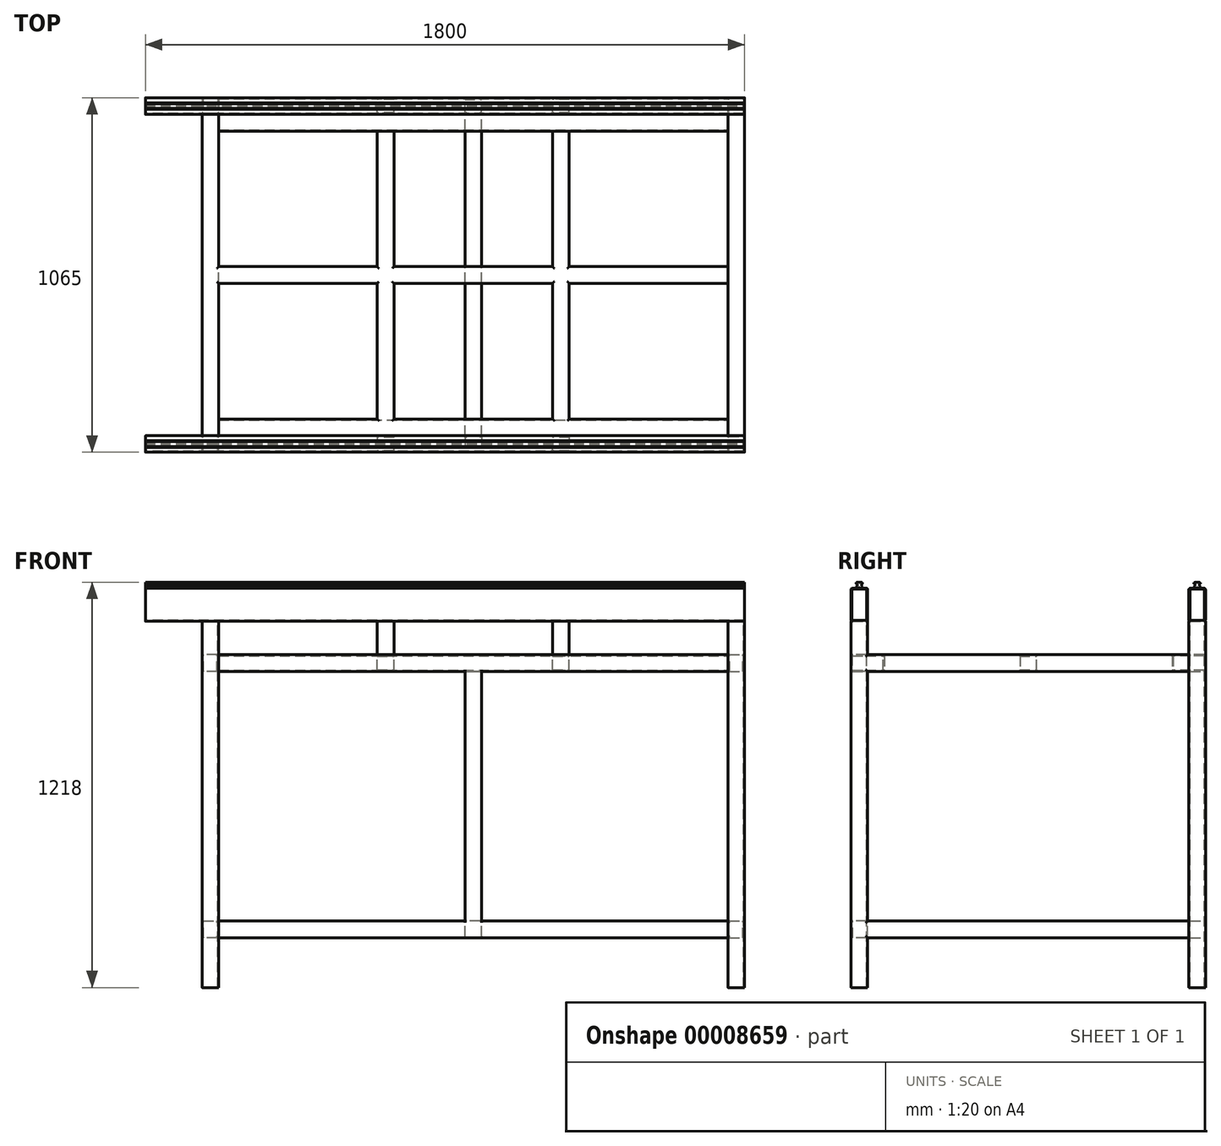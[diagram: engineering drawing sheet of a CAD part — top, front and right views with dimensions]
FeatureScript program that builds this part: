
annotation { "Feature Type Name" : "Feature", "Feature Type Description" : "" }
export const myFeature = defineFeature(function(context is Context, id is Id, definition is map)
    precondition{}
    {
        {
            var Q0;
            Q0=qCreatedBy(makeId("Right.planeOp"),FACE);
            var sketch = newSketch(context, id + "F0", { "sketchPlane" : qUnion([Q0])});
            skLineSegment(sketch, "E0.rect.bottom", {"start": v(20, 50) * mm, "end": v(-20, 50) * mm});
            skLineSegment(sketch, "E0.rect.top", {"start": v(20, -50) * mm, "end": v(-20, -50) * mm});
            skLineSegment(sketch, "E0.rect.left", {"start": v(25, 45) * mm, "end": v(25, -45) * mm});
            skLineSegment(sketch, "E0.rect.right", {"start": v(-25, 45) * mm, "end": v(-25, -45) * mm});
            skPoint(sketch, "E0.rect.middle", {"position": v(0, 0) * mm});
            skPoint(sketch, "E1.visualSharp", {"position": v(-25, 50) * mm});
            skArc(sketch, "E1.filletArc", {"start": v(-20, 50) * mm, "mid": v(-23.54, 48.54) * mm, "end": v(-25, 45) * mm});
            skPoint(sketch, "E2.visualSharp", {"position": v(25, 50) * mm});
            skArc(sketch, "E2.filletArc", {"start": v(25, 45) * mm, "mid": v(23.54, 48.54) * mm, "end": v(20, 50) * mm});
            skPoint(sketch, "E3.visualSharp", {"position": v(25, -50) * mm});
            skArc(sketch, "E3.filletArc", {"start": v(20, -50) * mm, "mid": v(23.54, -48.54) * mm, "end": v(25, -45) * mm});
            skPoint(sketch, "E4.visualSharp", {"position": v(-25, -50) * mm});
            skArc(sketch, "E4.filletArc", {"start": v(-25, -45) * mm, "mid": v(-23.54, -48.54) * mm, "end": v(-20, -50) * mm});
            skLineSegment(sketch, "E5.0", {"start": v(-22, 47) * mm, "end": v(-22, -47) * mm});
            skLineSegment(sketch, "E5.1", {"start": v(22, 47) * mm, "end": v(-22, 47) * mm});
            skLineSegment(sketch, "E5.2", {"start": v(22, 47) * mm, "end": v(22, -47) * mm});
            skLineSegment(sketch, "E5.3", {"start": v(22, -47) * mm, "end": v(-22, -47) * mm});
            skSolve(sketch);
        }
        {
            var Q0;
            Q0=qCreatedBy(makeId("Right.planeOp"),FACE);
            var sketch = newSketch(context, id + "F1", { "sketchPlane" : qUnion([Q0])});
            skLineSegment(sketch, "E6.rect.bottom", {"start": v(-995, 50) * mm, "end": v(-1035, 50) * mm});
            skLineSegment(sketch, "E6.rect.top", {"start": v(-995, -50) * mm, "end": v(-1035, -50) * mm});
            skLineSegment(sketch, "E6.rect.left", {"start": v(-990, 45) * mm, "end": v(-990, -45) * mm});
            skLineSegment(sketch, "E6.rect.right", {"start": v(-1040, 45) * mm, "end": v(-1040, -45) * mm});
            skPoint(sketch, "E6.rect.middle", {"position": v(0, 0) * mm});
            skPoint(sketch, "E7.visualSharp", {"position": v(-1040, 50) * mm});
            skArc(sketch, "E7.filletArc", {"start": v(-1035, 50) * mm, "mid": v(-1038.54, 48.54) * mm, "end": v(-1040, 45) * mm});
            skPoint(sketch, "E8.visualSharp", {"position": v(-990, 50) * mm});
            skArc(sketch, "E8.filletArc", {"start": v(-990, 45) * mm, "mid": v(-991.46, 48.54) * mm, "end": v(-995, 50) * mm});
            skPoint(sketch, "E9.visualSharp", {"position": v(-990, -50) * mm});
            skArc(sketch, "E9.filletArc", {"start": v(-995, -50) * mm, "mid": v(-991.46, -48.54) * mm, "end": v(-990, -45) * mm});
            skPoint(sketch, "E10.visualSharp", {"position": v(-1040, -50) * mm});
            skArc(sketch, "E10.filletArc", {"start": v(-1040, -45) * mm, "mid": v(-1038.54, -48.54) * mm, "end": v(-1035, -50) * mm});
            skLineSegment(sketch, "E11.0", {"start": v(-1037, 47) * mm, "end": v(-1037, -47) * mm});
            skLineSegment(sketch, "E11.1", {"start": v(-993, 47) * mm, "end": v(-1037, 47) * mm});
            skLineSegment(sketch, "E11.2", {"start": v(-993, 47) * mm, "end": v(-993, -47) * mm});
            skLineSegment(sketch, "E11.3", {"start": v(-993, -47) * mm, "end": v(-1037, -47) * mm});
            skSolve(sketch);
        }
        {
            var Q0;
            Q0=makeQuery(id+"F1.imprint","IMPRINT",FACE,{"disambiguationData":[TD([[makeQuery(id+"F1.imprint","IMPRINT",EDGE,{"derivedFrom":sQuery(id+"F1.wireOp",EDGE,"E6.rect.bottom")}),1.0]])]});
            var Q1;
            Q1=makeQuery(id+"F0.imprint","IMPRINT",FACE,{"disambiguationData":[TD([[makeQuery(id+"F0.imprint","IMPRINT",EDGE,{"derivedFrom":sQuery(id+"F0.wireOp",EDGE,"E0.rect.bottom")}),1.0]])]});
            extrude(context, id + "F2", {"entities" : qUnion([Q0, Q1]), "depth" : 1800 * mm});
        }
        {
            var Q0;
            Q0=makeQuery(id+"F2.opExtrude","CAP_FACE",FACE,{"disambiguationData":[OSD([sQuery(id+"F1.wireOp",EDGE,"E6.rect.bottom"),sQuery(id+"F1.wireOp",EDGE,"E6.rect.top"),sQuery(id+"F1.wireOp",EDGE,"E6.rect.left"),sQuery(id+"F1.wireOp",EDGE,"E6.rect.right"),sQuery(id+"F1.wireOp",EDGE,"E7.filletArc"),sQuery(id+"F1.wireOp",EDGE,"E8.filletArc"),sQuery(id+"F1.wireOp",EDGE,"E9.filletArc"),sQuery(id+"F1.wireOp",EDGE,"E10.filletArc"),sQuery(id+"F1.wireOp",EDGE,"E11.0"),sQuery(id+"F1.wireOp",EDGE,"E11.1"),sQuery(id+"F1.wireOp",EDGE,"E11.2"),sQuery(id+"F1.wireOp",EDGE,"E11.3")])],"isStart":false});
            cPlane(context, id + "F3", {"entities" : qUnion([Q0]), "cplaneType" : CPlaneType.OFFSET, "offset" : 50 * mm, "oppositeDirection" : true, "width" : 150 * mm, "height" : 150 * mm});
        }
        {
            var Q0;
            Q0=qCreatedBy(id+"F3.planeOp",FACE);
            var sketch = newSketch(context, id + "F4", { "sketchPlane" : qUnion([Q0])});
            skLineSegment(sketch, "E12.bottom", {"start": v(-1035, -150) * mm, "end": v(-945, -150) * mm});
            skLineSegment(sketch, "E12.top", {"start": v(-1035, -200) * mm, "end": v(-945, -200) * mm});
            skLineSegment(sketch, "E12.left", {"start": v(-1040, -155) * mm, "end": v(-1040, -195) * mm});
            skLineSegment(sketch, "E12.right", {"start": v(-940, -155) * mm, "end": v(-940, -195) * mm});
            skPoint(sketch, "E13.visualSharp", {"position": v(-1040, -150) * mm});
            skArc(sketch, "E13.filletArc", {"start": v(-1035, -150) * mm, "mid": v(-1038.54, -151.46) * mm, "end": v(-1040, -155) * mm});
            skPoint(sketch, "E14.visualSharp", {"position": v(-940, -150) * mm});
            skArc(sketch, "E14.filletArc", {"start": v(-940, -155) * mm, "mid": v(-941.46, -151.46) * mm, "end": v(-945, -150) * mm});
            skPoint(sketch, "E15.visualSharp", {"position": v(-940, -200) * mm});
            skArc(sketch, "E15.filletArc", {"start": v(-945, -200) * mm, "mid": v(-941.46, -198.54) * mm, "end": v(-940, -195) * mm});
            skPoint(sketch, "E16.visualSharp", {"position": v(-1040, -200) * mm});
            skArc(sketch, "E16.filletArc", {"start": v(-1040, -195) * mm, "mid": v(-1038.54, -198.54) * mm, "end": v(-1035, -200) * mm});
            skLineSegment(sketch, "E17.0", {"start": v(-995, -50) * mm, "end": v(-1035, -50) * mm});
            skLineSegment(sketch, "E18.0", {"start": v(-1040, 45) * mm, "end": v(-1040, -45) * mm});
            skLineSegment(sketch, "E19.0", {"start": v(-943, -153) * mm, "end": v(-943, -197) * mm});
            skLineSegment(sketch, "E19.1", {"start": v(-1037, -153) * mm, "end": v(-943, -153) * mm});
            skLineSegment(sketch, "E19.2", {"start": v(-1037, -153) * mm, "end": v(-1037, -197) * mm});
            skLineSegment(sketch, "E19.3", {"start": v(-1037, -197) * mm, "end": v(-943, -197) * mm});
            skLineSegment(sketch, "E20.bottom", {"start": v(20, -150) * mm, "end": v(-70, -150) * mm});
            skLineSegment(sketch, "E20.top", {"start": v(20, -200) * mm, "end": v(-70, -200) * mm});
            skLineSegment(sketch, "E20.left", {"start": v(25, -155) * mm, "end": v(25, -195) * mm});
            skLineSegment(sketch, "E20.right", {"start": v(-75, -155) * mm, "end": v(-75, -195) * mm});
            skPoint(sketch, "E21.0", {"position": v(25, -50) * mm});
            skPoint(sketch, "E22.visualSharp", {"position": v(-75, -150) * mm});
            skArc(sketch, "E22.filletArc", {"start": v(-70, -150) * mm, "mid": v(-73.54, -151.46) * mm, "end": v(-75, -155) * mm});
            skPoint(sketch, "E23.visualSharp", {"position": v(25, -200) * mm});
            skArc(sketch, "E23.filletArc", {"start": v(20, -200) * mm, "mid": v(23.54, -198.54) * mm, "end": v(25, -195) * mm});
            skPoint(sketch, "E24.visualSharp", {"position": v(25, -150) * mm});
            skArc(sketch, "E24.filletArc", {"start": v(25, -155) * mm, "mid": v(23.54, -151.46) * mm, "end": v(20, -150) * mm});
            skPoint(sketch, "E25.visualSharp", {"position": v(-75, -200) * mm});
            skArc(sketch, "E25.filletArc", {"start": v(-75, -195) * mm, "mid": v(-73.54, -198.54) * mm, "end": v(-70, -200) * mm});
            skLineSegment(sketch, "E26.0", {"start": v(22, -153) * mm, "end": v(-72, -153) * mm});
            skLineSegment(sketch, "E26.1", {"start": v(22, -153) * mm, "end": v(22, -197) * mm});
            skLineSegment(sketch, "E26.2", {"start": v(22, -197) * mm, "end": v(-72, -197) * mm});
            skLineSegment(sketch, "E26.3", {"start": v(-72, -153) * mm, "end": v(-72, -197) * mm});
            skSolve(sketch);
        }
        {
            var Q0;
            Q0=makeQuery(id+"F4.imprint","IMPRINT",FACE,{"disambiguationData":[TD([[makeQuery(id+"F4.imprint","IMPRINT",EDGE,{"derivedFrom":sQuery(id+"F4.wireOp",EDGE,"E12.bottom")}),-1.0]])]});
            var Q1;
            Q1=makeQuery(id+"F4.imprint","IMPRINT",FACE,{"disambiguationData":[TD([[makeQuery(id+"F4.imprint","IMPRINT",EDGE,{"derivedFrom":sQuery(id+"F4.wireOp",EDGE,"E20.bottom")}),1.0]])]});
            extrude(context, id + "F5", {"entities" : qUnion([Q0, Q1]), "oppositeDirection" : true, "depth" : 1530 * mm});
        }
        {
            var Q0;
            Q0=makeQuery(id+"F2.opExtrude","SWEPT_FACE",FACE,{"disambiguationData":[OSD([sQuery(id+"F1.wireOp",EDGE,"E6.rect.top")])]});
            cPlane(context, id + "F6", {"entities" : qUnion([Q0]), "cplaneType" : CPlaneType.OFFSET, "offset" : 0 * mm, "width" : 150 * mm, "height" : 150 * mm});
        }
        {
            var Q0;
            Q0=qCreatedBy(id+"F6.planeOp",FACE);
            var sketch = newSketch(context, id + "F7", { "sketchPlane" : qUnion([Q0])});
            skPoint(sketch, "E27.0", {"position": v(1800, 990) * mm});
            skPoint(sketch, "E28.0", {"position": v(1750, 1040) * mm});
            skLineSegment(sketch, "E29.bottom", {"start": v(1755, 1040) * mm, "end": v(1795, 1040) * mm});
            skLineSegment(sketch, "E29.top", {"start": v(1755, 990) * mm, "end": v(1795, 990) * mm});
            skLineSegment(sketch, "E29.left", {"start": v(1750, 1035) * mm, "end": v(1750, 995) * mm});
            skLineSegment(sketch, "E29.right", {"start": v(1800, 1035) * mm, "end": v(1800, 995) * mm});
            skPoint(sketch, "E30.visualSharp", {"position": v(1800, 1040) * mm});
            skArc(sketch, "E30.filletArc", {"start": v(1800, 1035) * mm, "mid": v(1798.54, 1038.54) * mm, "end": v(1795, 1040) * mm});
            skArc(sketch, "E31.filletArc", {"start": v(1795, 990) * mm, "mid": v(1798.54, 991.46) * mm, "end": v(1800, 995) * mm});
            skPoint(sketch, "E32.visualSharp", {"position": v(1750, 990) * mm});
            skArc(sketch, "E32.filletArc", {"start": v(1750, 995) * mm, "mid": v(1751.46, 991.46) * mm, "end": v(1755, 990) * mm});
            skArc(sketch, "E33.filletArc", {"start": v(1755, 1040) * mm, "mid": v(1751.46, 1038.54) * mm, "end": v(1750, 1035) * mm});
            skLineSegment(sketch, "E34.0", {"start": v(1797, 1037) * mm, "end": v(1797, 993) * mm});
            skLineSegment(sketch, "E34.1", {"start": v(1753, 1037) * mm, "end": v(1797, 1037) * mm});
            skLineSegment(sketch, "E34.2", {"start": v(1753, 1037) * mm, "end": v(1753, 993) * mm});
            skLineSegment(sketch, "E34.3", {"start": v(1753, 993) * mm, "end": v(1797, 993) * mm});
            skSolve(sketch);
        }
        {
            var Q0;
            Q0=makeQuery(id+"F7.imprint","IMPRINT",FACE,{"disambiguationData":[TD([[makeQuery(id+"F7.imprint","IMPRINT",EDGE,{"derivedFrom":sQuery(id+"F7.wireOp",EDGE,"E29.bottom")}),-1.0]])]});
            extrude(context, id + "F8", {"entities" : qUnion([Q0]), "operationType" : NewBodyOperationType.ADD, "depth" : 1100 * mm});
        }
        {
            var Q0;
            Q0=qCreatedBy(id+"F6.planeOp",FACE);
            var sketch = newSketch(context, id + "F9", { "sketchPlane" : qUnion([Q0])});
            skPoint(sketch, "E35.0", {"position": v(1800, -25) * mm});
            skPoint(sketch, "E36.0", {"position": v(1800, 25) * mm});
            skPoint(sketch, "E37.0", {"position": v(1750, -25) * mm});
            skLineSegment(sketch, "E38.bottom", {"start": v(1795, 25) * mm, "end": v(1755, 25) * mm});
            skLineSegment(sketch, "E38.top", {"start": v(1795, -25) * mm, "end": v(1755, -25) * mm});
            skLineSegment(sketch, "E38.left", {"start": v(1800, 20) * mm, "end": v(1800, -20) * mm});
            skLineSegment(sketch, "E38.right", {"start": v(1750, 20) * mm, "end": v(1750, -20) * mm});
            skArc(sketch, "E39.filletArc", {"start": v(1800, 20) * mm, "mid": v(1798.54, 23.54) * mm, "end": v(1795, 25) * mm});
            skPoint(sketch, "E40.visualSharp", {"position": v(1750, 25) * mm});
            skArc(sketch, "E40.filletArc", {"start": v(1755, 25) * mm, "mid": v(1751.46, 23.54) * mm, "end": v(1750, 20) * mm});
            skArc(sketch, "E41.filletArc", {"start": v(1750, -20) * mm, "mid": v(1751.46, -23.54) * mm, "end": v(1755, -25) * mm});
            skArc(sketch, "E42.filletArc", {"start": v(1795, -25) * mm, "mid": v(1798.54, -23.54) * mm, "end": v(1800, -20) * mm});
            skLineSegment(sketch, "E43.0", {"start": v(1797, 22) * mm, "end": v(1753, 22) * mm});
            skLineSegment(sketch, "E43.1", {"start": v(1797, 22) * mm, "end": v(1797, -22) * mm});
            skLineSegment(sketch, "E43.2", {"start": v(1797, -22) * mm, "end": v(1753, -22) * mm});
            skLineSegment(sketch, "E43.3", {"start": v(1753, 22) * mm, "end": v(1753, -22) * mm});
            skSolve(sketch);
        }
        {
            var Q0;
            Q0=makeQuery(id+"F9.imprint","IMPRINT",FACE,{"disambiguationData":[TD([[makeQuery(id+"F9.imprint","IMPRINT",EDGE,{"derivedFrom":sQuery(id+"F9.wireOp",EDGE,"E38.bottom")}),1.0]])]});
            extrude(context, id + "F10", {"entities" : qUnion([Q0]), "operationType" : NewBodyOperationType.ADD, "depth" : 1100 * mm});
        }
        {
            var Q0;
            Q0=qCreatedBy(id+"F6.planeOp",FACE);
            var sketch = newSketch(context, id + "F11", { "sketchPlane" : qUnion([Q0])});
            skPoint(sketch, "E44.0", {"position": v(220, 1040) * mm});
            skLineSegment(sketch, "E45.bottom", {"start": v(215, 1040) * mm, "end": v(175, 1040) * mm});
            skLineSegment(sketch, "E45.top", {"start": v(215, 990) * mm, "end": v(175, 990) * mm});
            skLineSegment(sketch, "E45.left", {"start": v(220, 1035) * mm, "end": v(220, 995) * mm});
            skLineSegment(sketch, "E45.right", {"start": v(170, 1035) * mm, "end": v(170, 995) * mm});
            skPoint(sketch, "E46.visualSharp", {"position": v(170, 1040) * mm});
            skArc(sketch, "E46.filletArc", {"start": v(175, 1040) * mm, "mid": v(171.46, 1038.54) * mm, "end": v(170, 1035) * mm});
            skArc(sketch, "E47.filletArc", {"start": v(220, 1035) * mm, "mid": v(218.54, 1038.54) * mm, "end": v(215, 1040) * mm});
            skPoint(sketch, "E48.visualSharp", {"position": v(220, 990) * mm});
            skArc(sketch, "E48.filletArc", {"start": v(215, 990) * mm, "mid": v(218.54, 991.46) * mm, "end": v(220, 995) * mm});
            skPoint(sketch, "E49.visualSharp", {"position": v(170, 990) * mm});
            skArc(sketch, "E49.filletArc", {"start": v(170, 995) * mm, "mid": v(171.46, 991.46) * mm, "end": v(175, 990) * mm});
            skLineSegment(sketch, "E50.0", {"start": v(217, 1037) * mm, "end": v(173, 1037) * mm});
            skLineSegment(sketch, "E50.1", {"start": v(217, 1037) * mm, "end": v(217, 993) * mm});
            skLineSegment(sketch, "E50.2", {"start": v(217, 993) * mm, "end": v(173, 993) * mm});
            skLineSegment(sketch, "E50.3", {"start": v(173, 1037) * mm, "end": v(173, 993) * mm});
            skSolve(sketch);
        }
        {
            var Q0;
            Q0=makeQuery(id+"F11.imprint","IMPRINT",FACE,{"disambiguationData":[TD([[makeQuery(id+"F11.imprint","IMPRINT",EDGE,{"derivedFrom":sQuery(id+"F11.wireOp",EDGE,"E45.bottom")}),1.0]])]});
            extrude(context, id + "F12", {"entities" : qUnion([Q0]), "operationType" : NewBodyOperationType.ADD, "depth" : 1100 * mm});
        }
        {
            var Q0;
            Q0=qCreatedBy(id+"F6.planeOp",FACE);
            var sketch = newSketch(context, id + "F13", { "sketchPlane" : qUnion([Q0])});
            skPoint(sketch, "E51.0", {"position": v(220, -25) * mm});
            skLineSegment(sketch, "E52.bottom", {"start": v(215, -25) * mm, "end": v(175, -25) * mm});
            skLineSegment(sketch, "E52.top", {"start": v(215, 25) * mm, "end": v(175, 25) * mm});
            skLineSegment(sketch, "E52.left", {"start": v(220, -20) * mm, "end": v(220, 20) * mm});
            skLineSegment(sketch, "E52.right", {"start": v(170, -20) * mm, "end": v(170, 20) * mm});
            skPoint(sketch, "E53.visualSharp", {"position": v(170, 25) * mm});
            skArc(sketch, "E53.filletArc", {"start": v(175, 25) * mm, "mid": v(171.46, 23.54) * mm, "end": v(170, 20) * mm});
            skPoint(sketch, "E54.visualSharp", {"position": v(170, -25) * mm});
            skArc(sketch, "E54.filletArc", {"start": v(170, -20) * mm, "mid": v(171.46, -23.54) * mm, "end": v(175, -25) * mm});
            skArc(sketch, "E55.filletArc", {"start": v(215, -25) * mm, "mid": v(218.54, -23.54) * mm, "end": v(220, -20) * mm});
            skPoint(sketch, "E56.visualSharp", {"position": v(220, 25) * mm});
            skArc(sketch, "E56.filletArc", {"start": v(220, 20) * mm, "mid": v(218.54, 23.54) * mm, "end": v(215, 25) * mm});
            skLineSegment(sketch, "E57.0", {"start": v(217, 22) * mm, "end": v(173, 22) * mm});
            skLineSegment(sketch, "E57.1", {"start": v(217, -22) * mm, "end": v(217, 22) * mm});
            skLineSegment(sketch, "E57.2", {"start": v(217, -22) * mm, "end": v(173, -22) * mm});
            skLineSegment(sketch, "E57.3", {"start": v(173, -22) * mm, "end": v(173, 22) * mm});
            skSolve(sketch);
        }
        {
            var Q0;
            Q0=makeQuery(id+"F13.imprint","IMPRINT",FACE,{"disambiguationData":[TD([[makeQuery(id+"F13.imprint","IMPRINT",EDGE,{"derivedFrom":sQuery(id+"F13.wireOp",EDGE,"E52.bottom")}),-1.0]])]});
            extrude(context, id + "F14", {"entities" : qUnion([Q0]), "operationType" : NewBodyOperationType.ADD, "depth" : 1100 * mm});
        }
        {
            var Q0;
            Q0=makeQuery(id+"F10.opExtrude","SWEPT_FACE",FACE,{"disambiguationData":[OSD([sQuery(id+"F9.wireOp",EDGE,"E38.bottom")])]});
            cPlane(context, id + "F15", {"entities" : qUnion([Q0]), "cplaneType" : CPlaneType.OFFSET, "offset" : 0 * mm, "width" : 150 * mm, "height" : 150 * mm});
        }
        {
            var Q0;
            Q0=qCreatedBy(id+"F15.planeOp",FACE);
            var sketch = newSketch(context, id + "F16", { "sketchPlane" : qUnion([Q0])});
            skPoint(sketch, "E58.0", {"position": v(1750, -150) * mm});
            skLineSegment(sketch, "E59.bottom", {"start": v(1755, -150) * mm, "end": v(1795, -150) * mm});
            skLineSegment(sketch, "E59.top", {"start": v(1755, -200) * mm, "end": v(1795, -200) * mm});
            skLineSegment(sketch, "E59.left", {"start": v(1750, -155) * mm, "end": v(1750, -195) * mm});
            skLineSegment(sketch, "E59.right", {"start": v(1800, -155) * mm, "end": v(1800, -195) * mm});
            skPoint(sketch, "E60.0", {"position": v(1750, -200) * mm});
            skArc(sketch, "E61.filletArc", {"start": v(1755, -150) * mm, "mid": v(1751.46, -151.46) * mm, "end": v(1750, -155) * mm});
            skArc(sketch, "E62.filletArc", {"start": v(1750, -195) * mm, "mid": v(1751.46, -198.54) * mm, "end": v(1755, -200) * mm});
            skPoint(sketch, "E63.visualSharp", {"position": v(1800, -200) * mm});
            skArc(sketch, "E63.filletArc", {"start": v(1795, -200) * mm, "mid": v(1798.54, -198.54) * mm, "end": v(1800, -195) * mm});
            skPoint(sketch, "E64.visualSharp", {"position": v(1800, -150) * mm});
            skArc(sketch, "E64.filletArc", {"start": v(1800, -155) * mm, "mid": v(1798.54, -151.46) * mm, "end": v(1795, -150) * mm});
            skSolve(sketch);
        }
        {
            var Q0;
            Q0=makeQuery(id+"F16.imprint","IMPRINT",FACE,{"disambiguationData":[TD([[makeQuery(id+"F16.imprint","IMPRINT",EDGE,{"derivedFrom":sQuery(id+"F16.wireOp",EDGE,"E59.bottom")}),-1.0]])]});
            extrude(context, id + "F17", {"entities" : qUnion([Q0]), "operationType" : NewBodyOperationType.ADD, "endBound" : BoundingType.UP_TO_NEXT, "depth" : 965 * mm});
        }
        {
            var Q0;
            Q0=qCreatedBy(id+"F15.planeOp",FACE);
            var sketch = newSketch(context, id + "F18", { "sketchPlane" : qUnion([Q0])});
            skPoint(sketch, "E65.0", {"position": v(220, -150) * mm});
            skPoint(sketch, "E66.0", {"position": v(220, -200) * mm});
            skLineSegment(sketch, "E67.bottom", {"start": v(215, -150) * mm, "end": v(175, -150) * mm});
            skLineSegment(sketch, "E67.top", {"start": v(215, -200) * mm, "end": v(175, -200) * mm});
            skLineSegment(sketch, "E67.left", {"start": v(220, -155) * mm, "end": v(220, -195) * mm});
            skLineSegment(sketch, "E67.right", {"start": v(170, -155) * mm, "end": v(170, -195) * mm});
            skPoint(sketch, "E68.visualSharp", {"position": v(170, -150) * mm});
            skArc(sketch, "E68.filletArc", {"start": v(175, -150) * mm, "mid": v(171.46, -151.46) * mm, "end": v(170, -155) * mm});
            skPoint(sketch, "E69.visualSharp", {"position": v(170, -200) * mm});
            skArc(sketch, "E69.filletArc", {"start": v(170, -195) * mm, "mid": v(171.46, -198.54) * mm, "end": v(175, -200) * mm});
            skArc(sketch, "E70.filletArc", {"start": v(215, -200) * mm, "mid": v(218.54, -198.54) * mm, "end": v(220, -195) * mm});
            skArc(sketch, "E71.filletArc", {"start": v(220, -155) * mm, "mid": v(218.54, -151.46) * mm, "end": v(215, -150) * mm});
            skSolve(sketch);
        }
        {
            var Q0;
            Q0=makeQuery(id+"F18.imprint","IMPRINT",FACE,{"disambiguationData":[TD([[makeQuery(id+"F18.imprint","IMPRINT",EDGE,{"derivedFrom":sQuery(id+"F18.wireOp",EDGE,"E67.bottom")}),1.0]])]});
            extrude(context, id + "F19", {"entities" : qUnion([Q0]), "operationType" : NewBodyOperationType.ADD, "endBound" : BoundingType.UP_TO_NEXT, "depth" : 965 * mm});
        }
        {
            var Q0;
            Q0=qCreatedBy(id+"F15.planeOp",FACE);
            var sketch = newSketch(context, id + "F20", { "sketchPlane" : qUnion([Q0])});
            skPoint(sketch, "E72.0", {"position": v(1800, -1150) * mm});
            skPoint(sketch, "E73.0", {"position": v(1750, -1150) * mm});
            skLineSegment(sketch, "E74.bottom", {"start": v(1750, -1150) * mm, "end": v(1800, -1150) * mm, "construction": true});
            skLineSegment(sketch, "E74.top", {"start": v(1750, -1000) * mm, "end": v(1800, -1000) * mm, "construction": true});
            skLineSegment(sketch, "E74.left", {"start": v(1750, -1150) * mm, "end": v(1750, -1000) * mm, "construction": true});
            skLineSegment(sketch, "E74.right", {"start": v(1800, -1150) * mm, "end": v(1800, -1000) * mm, "construction": true});
            skLineSegment(sketch, "E75.bottom", {"start": v(1755, -1000) * mm, "end": v(1795, -1000) * mm});
            skLineSegment(sketch, "E75.top", {"start": v(1755, -950) * mm, "end": v(1795, -950) * mm});
            skLineSegment(sketch, "E75.left", {"start": v(1750, -995) * mm, "end": v(1750, -955) * mm});
            skLineSegment(sketch, "E75.right", {"start": v(1800, -995) * mm, "end": v(1800, -955) * mm});
            skPoint(sketch, "E76.visualSharp", {"position": v(1800, -950) * mm});
            skArc(sketch, "E76.filletArc", {"start": v(1800, -955) * mm, "mid": v(1798.54, -951.46) * mm, "end": v(1795, -950) * mm});
            skPoint(sketch, "E77.visualSharp", {"position": v(1800, -1000) * mm});
            skArc(sketch, "E77.filletArc", {"start": v(1795, -1000) * mm, "mid": v(1798.54, -998.54) * mm, "end": v(1800, -995) * mm});
            skPoint(sketch, "E78.visualSharp", {"position": v(1750, -1000) * mm});
            skArc(sketch, "E78.filletArc", {"start": v(1750, -995) * mm, "mid": v(1751.46, -998.54) * mm, "end": v(1755, -1000) * mm});
            skPoint(sketch, "E79.visualSharp", {"position": v(1750, -950) * mm});
            skArc(sketch, "E79.filletArc", {"start": v(1755, -950) * mm, "mid": v(1751.46, -951.46) * mm, "end": v(1750, -955) * mm});
            skSolve(sketch);
        }
        {
            var Q0;
            Q0=makeQuery(id+"F20.imprint","IMPRINT",FACE,{"disambiguationData":[TD([[makeQuery(id+"F20.imprint","IMPRINT",EDGE,{"derivedFrom":sQuery(id+"F20.wireOp",EDGE,"E75.bottom")}),1.0]])]});
            extrude(context, id + "F21", {"entities" : qUnion([Q0]), "operationType" : NewBodyOperationType.ADD, "endBound" : BoundingType.UP_TO_NEXT, "depth" : 965 * mm});
        }
        {
            var Q0;
            Q0=qCreatedBy(id+"F15.planeOp",FACE);
            var sketch = newSketch(context, id + "F22", { "sketchPlane" : qUnion([Q0])});
            skPoint(sketch, "E80.0", {"position": v(220, -1150) * mm});
            skPoint(sketch, "E81.0", {"position": v(170, -1150) * mm});
            skLineSegment(sketch, "E82.bottom", {"start": v(170, -1150) * mm, "end": v(220, -1150) * mm, "construction": true});
            skLineSegment(sketch, "E82.top", {"start": v(170, -1000) * mm, "end": v(220, -1000) * mm, "construction": true});
            skLineSegment(sketch, "E82.left", {"start": v(170, -1150) * mm, "end": v(170, -1000) * mm, "construction": true});
            skLineSegment(sketch, "E82.right", {"start": v(220, -1150) * mm, "end": v(220, -1000) * mm, "construction": true});
            skLineSegment(sketch, "E83.bottom", {"start": v(175, -1000) * mm, "end": v(215, -1000) * mm});
            skLineSegment(sketch, "E83.top", {"start": v(175, -950) * mm, "end": v(215, -950) * mm});
            skLineSegment(sketch, "E83.left", {"start": v(170, -995) * mm, "end": v(170, -955) * mm});
            skLineSegment(sketch, "E83.right", {"start": v(220, -995) * mm, "end": v(220, -955) * mm});
            skPoint(sketch, "E84.visualSharp", {"position": v(220, -950) * mm});
            skArc(sketch, "E84.filletArc", {"start": v(220, -955) * mm, "mid": v(218.54, -951.46) * mm, "end": v(215, -950) * mm});
            skPoint(sketch, "E85.visualSharp", {"position": v(170, -950) * mm});
            skArc(sketch, "E85.filletArc", {"start": v(175, -950) * mm, "mid": v(171.46, -951.46) * mm, "end": v(170, -955) * mm});
            skPoint(sketch, "E86.visualSharp", {"position": v(170, -1000) * mm});
            skArc(sketch, "E86.filletArc", {"start": v(170, -995) * mm, "mid": v(171.46, -998.54) * mm, "end": v(175, -1000) * mm});
            skPoint(sketch, "E87.visualSharp", {"position": v(220, -1000) * mm});
            skArc(sketch, "E87.filletArc", {"start": v(215, -1000) * mm, "mid": v(218.54, -998.54) * mm, "end": v(220, -995) * mm});
            skSolve(sketch);
        }
        {
            var Q0;
            Q0=makeQuery(id+"F22.imprint","IMPRINT",FACE,{"disambiguationData":[TD([[makeQuery(id+"F22.imprint","IMPRINT",EDGE,{"derivedFrom":sQuery(id+"F22.wireOp",EDGE,"E83.bottom")}),1.0]])]});
            extrude(context, id + "F23", {"entities" : qUnion([Q0]), "operationType" : NewBodyOperationType.ADD, "endBound" : BoundingType.UP_TO_NEXT, "depth" : 965 * mm});
        }
        {
            var Q0;
            Q0=makeQuery(id+"F5.opExtrude","SWEPT_FACE",FACE,{"disambiguationData":[OSD([sQuery(id+"F4.wireOp",EDGE,"E20.right")])]});
            cPlane(context, id + "F24", {"entities" : qUnion([Q0]), "cplaneType" : CPlaneType.OFFSET, "offset" : 0 * mm, "width" : 150 * mm, "height" : 150 * mm});
        }
        {
            var Q0;
            Q0=qCreatedBy(id+"F24.planeOp",FACE);
            var sketch = newSketch(context, id + "F25", { "sketchPlane" : qUnion([Q0])});
            skPoint(sketch, "E88.0", {"position": v(220, -150) * mm});
            skPoint(sketch, "E89.0", {"position": v(220, -200) * mm});
            skLineSegment(sketch, "E90.bottom", {"start": v(220, -150) * mm, "end": v(696.67, -150) * mm, "construction": true});
            skLineSegment(sketch, "E90.top", {"start": v(220, -200) * mm, "end": v(696.67, -200) * mm, "construction": true});
            skLineSegment(sketch, "E90.left", {"start": v(220, -150) * mm, "end": v(220, -200) * mm, "construction": true});
            skLineSegment(sketch, "E90.right", {"start": v(696.67, -150) * mm, "end": v(696.67, -200) * mm, "construction": true});
            skLineSegment(sketch, "E91.bottom", {"start": v(701.67, -150) * mm, "end": v(741.67, -150) * mm});
            skLineSegment(sketch, "E91.top", {"start": v(701.67, -200) * mm, "end": v(741.67, -200) * mm});
            skLineSegment(sketch, "E91.left", {"start": v(696.67, -155) * mm, "end": v(696.67, -195) * mm});
            skLineSegment(sketch, "E91.right", {"start": v(746.67, -155) * mm, "end": v(746.67, -195) * mm});
            skLineSegment(sketch, "E92.bottom", {"start": v(746.67, -150) * mm, "end": v(1223.33, -150) * mm, "construction": true});
            skLineSegment(sketch, "E92.top", {"start": v(746.67, -200) * mm, "end": v(1223.33, -200) * mm, "construction": true});
            skLineSegment(sketch, "E92.left", {"start": v(746.67, -150) * mm, "end": v(746.67, -200) * mm, "construction": true});
            skLineSegment(sketch, "E92.right", {"start": v(1223.33, -150) * mm, "end": v(1223.33, -200) * mm, "construction": true});
            skLineSegment(sketch, "E93.bottom", {"start": v(1228.33, -150) * mm, "end": v(1268.33, -150) * mm});
            skLineSegment(sketch, "E93.top", {"start": v(1228.33, -200) * mm, "end": v(1268.33, -200) * mm});
            skLineSegment(sketch, "E93.left", {"start": v(1223.33, -155) * mm, "end": v(1223.33, -195) * mm});
            skLineSegment(sketch, "E93.right", {"start": v(1273.33, -155) * mm, "end": v(1273.33, -195) * mm});
            skPoint(sketch, "E94.0", {"position": v(1750, -200) * mm});
            skLineSegment(sketch, "E95.bottom", {"start": v(1750, -200) * mm, "end": v(1273.33, -200) * mm, "construction": true});
            skLineSegment(sketch, "E95.top", {"start": v(1750, -150) * mm, "end": v(1273.33, -150) * mm, "construction": true});
            skLineSegment(sketch, "E95.left", {"start": v(1750, -200) * mm, "end": v(1750, -150) * mm, "construction": true});
            skLineSegment(sketch, "E95.right", {"start": v(1273.33, -200) * mm, "end": v(1273.33, -150) * mm, "construction": true});
            skPoint(sketch, "E96.visualSharp", {"position": v(696.67, -150) * mm});
            skArc(sketch, "E96.filletArc", {"start": v(701.67, -150) * mm, "mid": v(698.13, -151.46) * mm, "end": v(696.67, -155) * mm});
            skPoint(sketch, "E97.visualSharp", {"position": v(746.67, -150) * mm});
            skArc(sketch, "E97.filletArc", {"start": v(746.67, -155) * mm, "mid": v(745.2, -151.46) * mm, "end": v(741.67, -150) * mm});
            skPoint(sketch, "E98.visualSharp", {"position": v(746.67, -200) * mm});
            skArc(sketch, "E98.filletArc", {"start": v(741.67, -200) * mm, "mid": v(745.2, -198.54) * mm, "end": v(746.67, -195) * mm});
            skPoint(sketch, "E99.visualSharp", {"position": v(696.67, -200) * mm});
            skArc(sketch, "E99.filletArc", {"start": v(696.67, -195) * mm, "mid": v(698.13, -198.54) * mm, "end": v(701.67, -200) * mm});
            skPoint(sketch, "E100.visualSharp", {"position": v(1223.33, -150) * mm});
            skArc(sketch, "E100.filletArc", {"start": v(1228.33, -150) * mm, "mid": v(1224.8, -151.46) * mm, "end": v(1223.33, -155) * mm});
            skPoint(sketch, "E101.visualSharp", {"position": v(1273.33, -150) * mm});
            skArc(sketch, "E101.filletArc", {"start": v(1273.33, -155) * mm, "mid": v(1271.87, -151.46) * mm, "end": v(1268.33, -150) * mm});
            skPoint(sketch, "E102.visualSharp", {"position": v(1273.33, -200) * mm});
            skArc(sketch, "E102.filletArc", {"start": v(1268.33, -200) * mm, "mid": v(1271.87, -198.54) * mm, "end": v(1273.33, -195) * mm});
            skPoint(sketch, "E103.visualSharp", {"position": v(1223.33, -200) * mm});
            skArc(sketch, "E103.filletArc", {"start": v(1223.33, -195) * mm, "mid": v(1224.8, -198.54) * mm, "end": v(1228.33, -200) * mm});
            skSolve(sketch);
        }
        {
            var Q0;
            Q0=makeQuery(id+"F25.imprint","IMPRINT",FACE,{"disambiguationData":[TD([[makeQuery(id+"F25.imprint","IMPRINT",EDGE,{"derivedFrom":sQuery(id+"F25.wireOp",EDGE,"E91.bottom")}),-1.0]])]});
            var Q1;
            Q1=makeQuery(id+"F25.imprint","IMPRINT",FACE,{"disambiguationData":[TD([[makeQuery(id+"F25.imprint","IMPRINT",EDGE,{"derivedFrom":sQuery(id+"F25.wireOp",EDGE,"E93.bottom")}),-1.0]])]});
            extrude(context, id + "F26", {"entities" : qUnion([Q0, Q1]), "operationType" : NewBodyOperationType.ADD, "endBound" : BoundingType.UP_TO_NEXT, "depth" : 865 * mm});
        }
        {
            var Q0;
            {var subQ0=sQuery(id+"F11.wireOp",EDGE,"E45.left");var subQ4=sQuery(id+"F4.wireOp",EDGE,"E12.top");Q0=makeQuery(id+"F23.boolean.opBoolean","MERGE",FACE,{"derivedFrom":[makeQuery(id+"F12.boolean.opBoolean","SPLIT",FACE,{"disambiguationData":[TD([makeQuery(id+"F5.opExtrude","SWEPT_FACE",FACE,{"disambiguationData":[OSD([subQ4])]})])],"derivedFrom":makeQuery(id+"F12.opExtrude","SWEPT_FACE",FACE,{"disambiguationData":[OSD([subQ0])]})}),makeQuery(id+"F23.opExtrude","SWEPT_FACE",FACE,{"disambiguationData":[OSD([sQuery(id+"F22.wireOp",EDGE,"E83.right")])]})]});}
            cPlane(context, id + "F27", {"entities" : qUnion([Q0]), "cplaneType" : CPlaneType.OFFSET, "offset" : 10 * mm, "width" : 150 * mm, "height" : 150 * mm});
        }
        {
            var Q0;
            Q0=qCreatedBy(id+"F27.planeOp",FACE);
            var sketch = newSketch(context, id + "F28", { "sketchPlane" : qUnion([Q0])});
            skPoint(sketch, "E104.0", {"position": v(-990, -1000) * mm});
            skPoint(sketch, "E105.0", {"position": v(-990, -950) * mm});
            skLineSegment(sketch, "E106.bottom", {"start": v(-995, -950) * mm, "end": v(-1035, -950) * mm});
            skLineSegment(sketch, "E106.top", {"start": v(-995, -1000) * mm, "end": v(-1035, -1000) * mm});
            skLineSegment(sketch, "E106.left", {"start": v(-990, -955) * mm, "end": v(-990, -995) * mm});
            skLineSegment(sketch, "E106.right", {"start": v(-1040, -955) * mm, "end": v(-1040, -995) * mm});
            skArc(sketch, "E107.filletArc", {"start": v(-990, -955) * mm, "mid": v(-991.46, -951.46) * mm, "end": v(-995, -950) * mm});
            skPoint(sketch, "E108.visualSharp", {"position": v(-1040, -950) * mm});
            skArc(sketch, "E108.filletArc", {"start": v(-1035, -950) * mm, "mid": v(-1038.54, -951.46) * mm, "end": v(-1040, -955) * mm});
            skPoint(sketch, "E109.visualSharp", {"position": v(-1040, -1000) * mm});
            skArc(sketch, "E109.filletArc", {"start": v(-1040, -995) * mm, "mid": v(-1038.54, -998.54) * mm, "end": v(-1035, -1000) * mm});
            skArc(sketch, "E110.filletArc", {"start": v(-995, -1000) * mm, "mid": v(-991.46, -998.54) * mm, "end": v(-990, -995) * mm});
            skSolve(sketch);
        }
        {
            var Q0;
            Q0 = qSketchRegion(id + "F28", true);
            var Q1;
            Q1=makeQuery(id+"F8.opExtrude","SWEPT_FACE",FACE,{"disambiguationData":[OSD([sQuery(id+"F7.wireOp",EDGE,"E29.left")])]});
            var Q2;
            Q2=makeQuery(id+"F12.opExtrude","SWEPT_FACE",FACE,{"disambiguationData":[OSD([sQuery(id+"F11.wireOp",EDGE,"E45.left")])]});
            extrude(context, id + "F29", {"entities" : qUnion([Q0]), "operationType" : NewBodyOperationType.ADD, "endBound" : BoundingType.UP_TO_SURFACE, "endBoundEntityFace" : qUnion([Q1]), "depth" : 1530 * mm, "hasSecondDirection" : true, "secondDirectionBound" : SecondDirectionBoundingType.UP_TO_SURFACE, "secondDirectionOppositeDirection" : true, "secondDirectionBoundEntityFace" : qUnion([Q2]), "secondDirectionDepth" : 25 * mm});
        }
        {
            var Q0;
            Q0=qCreatedBy(id+"F27.planeOp",FACE);
            var sketch = newSketch(context, id + "F30", { "sketchPlane" : qUnion([Q0])});
            skPoint(sketch, "E111.0", {"position": v(-25, -1000) * mm});
            skPoint(sketch, "E112.0", {"position": v(-25, -950) * mm});
            skLineSegment(sketch, "E113.bottom", {"start": v(-20, -950) * mm, "end": v(20, -950) * mm});
            skLineSegment(sketch, "E113.top", {"start": v(-20, -1000) * mm, "end": v(20, -1000) * mm});
            skLineSegment(sketch, "E113.left", {"start": v(-25, -955) * mm, "end": v(-25, -995) * mm});
            skLineSegment(sketch, "E113.right", {"start": v(25, -955) * mm, "end": v(25, -995) * mm});
            skArc(sketch, "E114.filletArc", {"start": v(-20, -950) * mm, "mid": v(-23.54, -951.46) * mm, "end": v(-25, -955) * mm});
            skPoint(sketch, "E115.visualSharp", {"position": v(25, -950) * mm});
            skArc(sketch, "E115.filletArc", {"start": v(25, -955) * mm, "mid": v(23.54, -951.46) * mm, "end": v(20, -950) * mm});
            skPoint(sketch, "E116.visualSharp", {"position": v(25, -1000) * mm});
            skArc(sketch, "E116.filletArc", {"start": v(20, -1000) * mm, "mid": v(23.54, -998.54) * mm, "end": v(25, -995) * mm});
            skArc(sketch, "E117.filletArc", {"start": v(-25, -995) * mm, "mid": v(-23.54, -998.54) * mm, "end": v(-20, -1000) * mm});
            skSolve(sketch);
        }
        {
            var Q0;
            Q0=makeQuery(id+"F30.imprint","IMPRINT",FACE,{"disambiguationData":[TD([[makeQuery(id+"F30.imprint","IMPRINT",EDGE,{"derivedFrom":sQuery(id+"F30.wireOp",EDGE,"E113.bottom")}),-1.0]])]});
            var Q1;
            {var subQ0=sQuery(id+"F9.wireOp",EDGE,"E38.right");var subQ4=sQuery(id+"F4.wireOp",EDGE,"E20.top");Q1=makeQuery(id+"Fz8Vrk44a0iJE9b_11.opBoolean","SPLIT",FACE,{"disambiguationData":[TD([makeQuery(id+"F5.opExtrude","SWEPT_FACE",FACE,{"disambiguationData":[OSD([subQ4])]})])],"derivedFrom":makeQuery(id+"F10.opExtrude","SWEPT_FACE",FACE,{"disambiguationData":[OSD([subQ0])]})});}
            var Q2;
            {var subQ0=sQuery(id+"F13.wireOp",EDGE,"E52.left");var subQ4=sQuery(id+"F4.wireOp",EDGE,"E20.top");Q2=makeQuery(id+"Fz8Vrk44a0iJE9b_11.opBoolean","SPLIT",FACE,{"disambiguationData":[TD([makeQuery(id+"F5.opExtrude","SWEPT_FACE",FACE,{"disambiguationData":[OSD([subQ4])]})])],"derivedFrom":makeQuery(id+"F14.opExtrude","SWEPT_FACE",FACE,{"disambiguationData":[OSD([subQ0])]})});}
            extrude(context, id + "F31", {"entities" : qUnion([Q0]), "operationType" : NewBodyOperationType.ADD, "endBound" : BoundingType.UP_TO_NEXT, "endBoundEntity" : qUnion([Q1]), "depth" : 25 * mm, "hasSecondDirection" : true, "secondDirectionBound" : SecondDirectionBoundingType.UP_TO_NEXT, "secondDirectionOppositeDirection" : true, "secondDirectionBoundEntity" : qUnion([Q2]), "secondDirectionDepth" : 25 * mm});
        }
        {
            var Q0;
            Q0=makeQuery(id+"F23.opExtrude","SWEPT_FACE",FACE,{"disambiguationData":[OSD([sQuery(id+"F22.wireOp",EDGE,"E83.top")])]});
            cPlane(context, id + "F32", {"entities" : qUnion([Q0]), "cplaneType" : CPlaneType.OFFSET, "offset" : 500 * mm, "width" : 150 * mm, "height" : 150 * mm});
        }
        {
            var Q0;
            Q0=qCreatedBy(id+"F32.planeOp",FACE);
            var sketch = newSketch(context, id + "F33", { "sketchPlane" : qUnion([Q0])});
            skPoint(sketch, "E118.0", {"position": v(220, -1040) * mm});
            skPoint(sketch, "E119.0", {"position": v(1750, -990) * mm});
            skLineSegment(sketch, "E120.bottom", {"start": v(220, -1040) * mm, "end": v(1750, -1040) * mm, "construction": true});
            skLineSegment(sketch, "E120.top", {"start": v(220, -990) * mm, "end": v(1750, -990) * mm, "construction": true});
            skLineSegment(sketch, "E120.left", {"start": v(220, -1040) * mm, "end": v(220, -990) * mm, "construction": true});
            skLineSegment(sketch, "E120.right", {"start": v(1750, -1040) * mm, "end": v(1750, -990) * mm, "construction": true});
            skPoint(sketch, "E121", {"position": v(985, -1040) * mm});
            skLineSegment(sketch, "E122.bottom", {"start": v(960, -1040) * mm, "end": v(1010, -1040) * mm});
            skLineSegment(sketch, "E122.top", {"start": v(960, -990) * mm, "end": v(1010, -990) * mm});
            skLineSegment(sketch, "E122.left", {"start": v(960, -1040) * mm, "end": v(960, -990) * mm});
            skLineSegment(sketch, "E122.right", {"start": v(1010, -1040) * mm, "end": v(1010, -990) * mm});
            skSolve(sketch);
        }
        {
            var Q0;
            Q0=makeQuery(id+"F33.imprint","IMPRINT",FACE,{"disambiguationData":[TD([[makeQuery(id+"F33.imprint","IMPRINT",EDGE,{"derivedFrom":sQuery(id+"F33.wireOp",EDGE,"E122.bottom")}),1.0]])]});
            var Q1;
            Q1=makeQuery(id+"F26.boolean.opBoolean","MERGE",FACE,{"derivedFrom":[makeQuery(id+"F5.opExtrude","SWEPT_FACE",FACE,{"disambiguationData":[OSD([sQuery(id+"F4.wireOp",EDGE,"E12.top")])]}),makeQuery(id+"F26.opExtrude","SWEPT_FACE",FACE,{"disambiguationData":[OSD([sQuery(id+"F25.wireOp",EDGE,"E91.top")])]}),makeQuery(id+"F26.opExtrude","SWEPT_FACE",FACE,{"disambiguationData":[OSD([sQuery(id+"F25.wireOp",EDGE,"E93.top")])]})]});
            var Q2;
            Q2=makeQuery(id+"F29.opExtrude","SWEPT_FACE",FACE,{"disambiguationData":[OSD([sQuery(id+"F28.wireOp",EDGE,"E106.bottom")])]});
            extrude(context, id + "F34", {"entities" : qUnion([Q0]), "operationType" : NewBodyOperationType.ADD, "endBound" : BoundingType.UP_TO_NEXT, "endBoundEntity" : qUnion([Q1]), "depth" : 25 * mm, "hasSecondDirection" : true, "secondDirectionBound" : SecondDirectionBoundingType.UP_TO_NEXT, "secondDirectionOppositeDirection" : true, "secondDirectionBoundEntity" : qUnion([Q2]), "secondDirectionDepth" : 25 * mm});
        }
        {
            var Q0;
            Q0=qCreatedBy(id+"F32.planeOp",FACE);
            var sketch = newSketch(context, id + "F35", { "sketchPlane" : qUnion([Q0])});
            skPoint(sketch, "E123.0", {"position": v(220, 20) * mm});
            skPoint(sketch, "E124.0", {"position": v(1750, -20) * mm});
            skLineSegment(sketch, "E125.bottom", {"start": v(1750, -20) * mm, "end": v(220, -20) * mm, "construction": true});
            skLineSegment(sketch, "E125.top", {"start": v(1750, 20) * mm, "end": v(220, 20) * mm, "construction": true});
            skLineSegment(sketch, "E125.left", {"start": v(1750, -20) * mm, "end": v(1750, 20) * mm, "construction": true});
            skLineSegment(sketch, "E125.right", {"start": v(220, -20) * mm, "end": v(220, 20) * mm, "construction": true});
            skPoint(sketch, "E126", {"position": v(985, 20) * mm});
            skLineSegment(sketch, "E127.bottom", {"start": v(1005, -25) * mm, "end": v(965, -25) * mm});
            skLineSegment(sketch, "E127.top", {"start": v(1005, 25) * mm, "end": v(965, 25) * mm});
            skLineSegment(sketch, "E127.left", {"start": v(1010, -20) * mm, "end": v(1010, 20) * mm});
            skLineSegment(sketch, "E127.right", {"start": v(960, -20) * mm, "end": v(960, 20) * mm});
            skPoint(sketch, "E128.visualSharp", {"position": v(1010, 25) * mm});
            skArc(sketch, "E128.filletArc", {"start": v(1010, 20) * mm, "mid": v(1008.54, 23.54) * mm, "end": v(1005, 25) * mm});
            skPoint(sketch, "E129.visualSharp", {"position": v(1010, -25) * mm});
            skArc(sketch, "E129.filletArc", {"start": v(1005, -25) * mm, "mid": v(1008.54, -23.54) * mm, "end": v(1010, -20) * mm});
            skPoint(sketch, "E130.visualSharp", {"position": v(960, -25) * mm});
            skArc(sketch, "E130.filletArc", {"start": v(960, -20) * mm, "mid": v(961.46, -23.54) * mm, "end": v(965, -25) * mm});
            skPoint(sketch, "E131.visualSharp", {"position": v(960, 25) * mm});
            skArc(sketch, "E131.filletArc", {"start": v(965, 25) * mm, "mid": v(961.46, 23.54) * mm, "end": v(960, 20) * mm});
            skLineSegment(sketch, "E132", {"start": v(1010, 20) * mm, "end": v(960, 20) * mm, "construction": true});
            skSolve(sketch);
        }
        {
            var Q0;
            Q0=makeQuery(id+"F35.imprint","IMPRINT",FACE,{"disambiguationData":[TD([[makeQuery(id+"F35.imprint","IMPRINT",EDGE,{"derivedFrom":sQuery(id+"F35.wireOp",EDGE,"E127.bottom")}),-1.0]])]});
            var Q1;
            Q1=makeQuery(id+"F5.opExtrude","SWEPT_FACE",FACE,{"disambiguationData":[OSD([sQuery(id+"F4.wireOp",EDGE,"E20.top")])]});
            var Q2;
            Q2=makeQuery(id+"F31.opExtrude","SWEPT_FACE",FACE,{"disambiguationData":[OSD([sQuery(id+"F30.wireOp",EDGE,"E113.bottom")])]});
            extrude(context, id + "F36", {"entities" : qUnion([Q0]), "operationType" : NewBodyOperationType.ADD, "endBound" : BoundingType.UP_TO_SURFACE, "endBoundEntityFace" : qUnion([Q1]), "depth" : 25 * mm, "hasSecondDirection" : true, "secondDirectionBound" : SecondDirectionBoundingType.UP_TO_SURFACE, "secondDirectionOppositeDirection" : true, "secondDirectionBoundEntityFace" : qUnion([Q2]), "secondDirectionDepth" : 25 * mm});
        }
        {
            var Q0;
            {var subQ5=sQuery(id+"F4.wireOp",EDGE,"E12.right");Q0=makeQuery(id+"F19.boolean.opBoolean","SPLIT",FACE,{"disambiguationData":[TD([makeQuery(id+"F5.opExtrude","SWEPT_FACE",FACE,{"disambiguationData":[OSD([subQ5])]})])],"derivedFrom":makeQuery(id+"F19.opExtrude","SWEPT_FACE",FACE,{"disambiguationData":[OSD([sQuery(id+"F18.wireOp",EDGE,"E67.left")])]})});}
            cPlane(context, id + "F37", {"entities" : qUnion([Q0]), "cplaneType" : CPlaneType.OFFSET, "offset" : 150 * mm, "width" : 150 * mm, "height" : 150 * mm});
        }
        {
            var Q0;
            Q0=qCreatedBy(id+"F37.planeOp",FACE);
            var sketch = newSketch(context, id + "F38", { "sketchPlane" : qUnion([Q0])});
            skPoint(sketch, "E133.0", {"position": v(-945, -150) * mm});
            skPoint(sketch, "E134.0", {"position": v(-70, -200) * mm});
            skLineSegment(sketch, "E135.bottom", {"start": v(-945, -150) * mm, "end": v(-70, -150) * mm, "construction": true});
            skLineSegment(sketch, "E135.top", {"start": v(-945, -200) * mm, "end": v(-70, -200) * mm, "construction": true});
            skLineSegment(sketch, "E135.left", {"start": v(-945, -150) * mm, "end": v(-945, -200) * mm, "construction": true});
            skLineSegment(sketch, "E135.right", {"start": v(-70, -150) * mm, "end": v(-70, -200) * mm, "construction": true});
            skPoint(sketch, "E136", {"position": v(-507.5, -200) * mm});
            skLineSegment(sketch, "E137.bottom", {"start": v(-527.5, -150) * mm, "end": v(-487.5, -150) * mm});
            skLineSegment(sketch, "E137.top", {"start": v(-527.5, -200) * mm, "end": v(-487.5, -200) * mm});
            skLineSegment(sketch, "E137.left", {"start": v(-532.5, -155) * mm, "end": v(-532.5, -195) * mm});
            skLineSegment(sketch, "E137.right", {"start": v(-482.5, -155) * mm, "end": v(-482.5, -195) * mm});
            skPoint(sketch, "E138.visualSharp", {"position": v(-532.5, -150) * mm});
            skArc(sketch, "E138.filletArc", {"start": v(-527.5, -150) * mm, "mid": v(-531.04, -151.46) * mm, "end": v(-532.5, -155) * mm});
            skPoint(sketch, "E139.visualSharp", {"position": v(-482.5, -150) * mm});
            skArc(sketch, "E139.filletArc", {"start": v(-482.5, -155) * mm, "mid": v(-483.96, -151.46) * mm, "end": v(-487.5, -150) * mm});
            skPoint(sketch, "E140.visualSharp", {"position": v(-482.5, -200) * mm});
            skArc(sketch, "E140.filletArc", {"start": v(-487.5, -200) * mm, "mid": v(-483.96, -198.54) * mm, "end": v(-482.5, -195) * mm});
            skPoint(sketch, "E141.visualSharp", {"position": v(-532.5, -200) * mm});
            skArc(sketch, "E141.filletArc", {"start": v(-532.5, -195) * mm, "mid": v(-531.04, -198.54) * mm, "end": v(-527.5, -200) * mm});
            skSolve(sketch);
        }
        {
            var Q0;
            Q0=makeQuery(id+"F38.imprint","IMPRINT",FACE,{"disambiguationData":[TD([[makeQuery(id+"F38.imprint","IMPRINT",EDGE,{"derivedFrom":sQuery(id+"F38.wireOp",EDGE,"E137.bottom")}),-1.0]])]});
            var Q1;
            {var subQ3=sQuery(id+"F4.wireOp",EDGE,"E12.right");Q1=makeQuery(id+"F17.boolean.opBoolean","SPLIT",FACE,{"disambiguationData":[TD([makeQuery(id+"F5.opExtrude","SWEPT_FACE",FACE,{"disambiguationData":[OSD([subQ3])]})])],"derivedFrom":makeQuery(id+"F17.opExtrude","SWEPT_FACE",FACE,{"disambiguationData":[OSD([sQuery(id+"F16.wireOp",EDGE,"E59.left")])]})});}
            extrude(context, id + "F39", {"entities" : qUnion([Q0]), "operationType" : NewBodyOperationType.ADD, "endBound" : BoundingType.UP_TO_SURFACE, "endBoundEntityFace" : qUnion([Q1]), "depth" : 25 * mm, "hasSecondDirection" : true, "secondDirectionBound" : SecondDirectionBoundingType.UP_TO_NEXT, "secondDirectionOppositeDirection" : true, "secondDirectionDepth" : 25 * mm});
        }
        {
            var Q0;
            Q0=makeQuery(id+"F21.boolean.opBoolean","MERGE",FACE,{"derivedFrom":[makeQuery(id+"F17.boolean.opBoolean","MERGE",FACE,{"derivedFrom":[makeQuery(id+"F8.boolean.opBoolean","MERGE",FACE,{"derivedFrom":[makeQuery(id+"F2.opExtrude","CAP_FACE",FACE,{"disambiguationData":[OSD([sQuery(id+"F1.wireOp",EDGE,"E6.rect.bottom"),sQuery(id+"F1.wireOp",EDGE,"E6.rect.top"),sQuery(id+"F1.wireOp",EDGE,"E6.rect.left"),sQuery(id+"F1.wireOp",EDGE,"E6.rect.right"),sQuery(id+"F1.wireOp",EDGE,"E7.filletArc"),sQuery(id+"F1.wireOp",EDGE,"E8.filletArc"),sQuery(id+"F1.wireOp",EDGE,"E9.filletArc"),sQuery(id+"F1.wireOp",EDGE,"E10.filletArc"),sQuery(id+"F1.wireOp",EDGE,"E11.0"),sQuery(id+"F1.wireOp",EDGE,"E11.1"),sQuery(id+"F1.wireOp",EDGE,"E11.2"),sQuery(id+"F1.wireOp",EDGE,"E11.3")])],"isStart":false}),makeQuery(id+"F8.opExtrude","SWEPT_FACE",FACE,{"disambiguationData":[OSD([sQuery(id+"F7.wireOp",EDGE,"E29.right")])]})]}),makeQuery(id+"F17.opExtrude","SWEPT_FACE",FACE,{"disambiguationData":[OSD([sQuery(id+"F16.wireOp",EDGE,"E59.right")])]})]}),makeQuery(id+"F21.opExtrude","SWEPT_FACE",FACE,{"disambiguationData":[OSD([sQuery(id+"F20.wireOp",EDGE,"E75.right")])]})]});
            cPlane(context, id + "F40", {"entities" : qUnion([Q0]), "cplaneType" : CPlaneType.OFFSET, "offset" : 0 * mm, "width" : 150 * mm, "height" : 150 * mm});
        }
        {
            var Q0;
            Q0=qCreatedBy(id+"F40.planeOp",FACE);
            var sketch = newSketch(context, id + "F41", { "sketchPlane" : qUnion([Q0])});
            skLineSegment(sketch, "E142.0", {"start": v(-995, 50) * mm, "end": v(-1035, 50) * mm, "construction": true});
            skPoint(sketch, "E143", {"position": v(-1015, 50) * mm});
            skLineSegment(sketch, "E144.0", {"start": v(20, 50) * mm, "end": v(-20, 50) * mm, "construction": true});
            skPoint(sketch, "E145", {"position": v(0, 50) * mm});
            skLineSegment(sketch, "E146.bottom", {"start": v(-10, 50) * mm, "end": v(10, 50) * mm, "construction": true});
            skLineSegment(sketch, "E146.top", {"start": v(-10, 68) * mm, "end": v(10, 68) * mm, "construction": true});
            skLineSegment(sketch, "E146.left", {"start": v(-10, 50) * mm, "end": v(-10, 68) * mm, "construction": true});
            skLineSegment(sketch, "E146.right", {"start": v(10, 50) * mm, "end": v(10, 68) * mm, "construction": true});
            skLineSegment(sketch, "E147", {"start": v(-10, 64.5) * mm, "end": v(10, 64.5) * mm, "construction": true});
            skPoint(sketch, "E148", {"position": v(0, 64.5) * mm});
            skLineSegment(sketch, "E149.rect.bottom", {"start": v(20, 67.5) * mm, "end": v(-10, 67.5) * mm, "construction": true});
            skLineSegment(sketch, "E149.rect.top", {"start": v(10, 61.5) * mm, "end": v(-20, 61.5) * mm, "construction": true});
            skArc(sketch, "E150", {"start": v(-10, 65.4) * mm, "mid": v(-8.52, 66.02) * mm, "end": v(-7.9, 67.5) * mm});
            skArc(sketch, "E151.0.MirrorCS", {"start": v(-10, 63.6) * mm, "mid": v(-8.52, 62.98) * mm, "end": v(-7.9, 61.5) * mm});
            skLineSegment(sketch, "E152", {"start": v(0, 64.5) * mm, "end": v(0, 50) * mm, "construction": true});
            skArc(sketch, "E153.0.MirrorCS", {"start": v(10, 63.6) * mm, "mid": v(8.52, 62.98) * mm, "end": v(7.9, 61.5) * mm});
            skArc(sketch, "E153.1.MirrorCS", {"start": v(10, 65.4) * mm, "mid": v(8.52, 66.02) * mm, "end": v(7.9, 67.5) * mm});
            skLineSegment(sketch, "E154", {"start": v(-7.9, 67.5) * mm, "end": v(-7.4, 68) * mm});
            skLineSegment(sketch, "E155", {"start": v(-7.4, 68) * mm, "end": v(7.4, 68) * mm});
            skLineSegment(sketch, "E156", {"start": v(7.4, 68) * mm, "end": v(7.9, 67.5) * mm});
            skPoint(sketch, "E157", {"position": v(0, 68) * mm});
            skLineSegment(sketch, "E158.bottom", {"start": v(-6.55, 60.5) * mm, "end": v(6.55, 60.5) * mm, "construction": true});
            skLineSegment(sketch, "E158.top", {"start": v(-6.55, 57.5) * mm, "end": v(6.55, 57.5) * mm, "construction": true});
            skLineSegment(sketch, "E158.left", {"start": v(-6.55, 60.5) * mm, "end": v(-6.55, 57.5) * mm, "construction": true});
            skLineSegment(sketch, "E158.right", {"start": v(6.55, 60.5) * mm, "end": v(6.55, 57.5) * mm, "construction": true});
            skPoint(sketch, "E159", {"position": v(0, 57.5) * mm});
            skLineSegment(sketch, "E160", {"start": v(-7.9, 61.5) * mm, "end": v(-6.55, 60.5) * mm});
            skLineSegment(sketch, "E161", {"start": v(6.55, 60.5) * mm, "end": v(7.9, 61.5) * mm});
            skLineSegment(sketch, "E162", {"start": v(6.55, 60.5) * mm, "end": v(6.55, 57.5) * mm});
            skLineSegment(sketch, "E163", {"start": v(-6.55, 57.5) * mm, "end": v(-6.55, 60.5) * mm});
            skLineSegment(sketch, "E164", {"start": v(-10, 54) * mm, "end": v(-10, 50.5) * mm});
            skLineSegment(sketch, "E165", {"start": v(-9.5, 50) * mm, "end": v(-2, 50) * mm});
            skLineSegment(sketch, "E166", {"start": v(10, 50.5) * mm, "end": v(10, 54) * mm});
            skLineSegment(sketch, "E167", {"start": v(-6.55, 57.5) * mm, "end": v(-10, 54) * mm});
            skLineSegment(sketch, "E168", {"start": v(10, 54) * mm, "end": v(6.55, 57.5) * mm});
            skCircle(sketch, "E169", {"center": v(-10, 50) * mm, "radius": 0.5 * mm, "construction": true});
            skCircle(sketch, "E170", {"center": v(10, 50) * mm, "radius": 0.5 * mm, "construction": true});
            skLineSegment(sketch, "E171", {"start": v(-10, 50.5) * mm, "end": v(-9.5, 50) * mm});
            skLineSegment(sketch, "E172", {"start": v(10, 50.5) * mm, "end": v(9.5, 50) * mm});
            skLineSegment(sketch, "E173.trimOffspring", {"start": v(2, 50) * mm, "end": v(9.5, 50) * mm});
            skLineSegment(sketch, "E174", {"start": v(-1.5, 50.5) * mm, "end": v(1.5, 50.5) * mm});
            skPoint(sketch, "E175", {"position": v(0, 50.5) * mm});
            skLineSegment(sketch, "E176", {"start": v(2, 50) * mm, "end": v(1.5, 50.5) * mm});
            skLineSegment(sketch, "E177", {"start": v(-1.5, 50.5) * mm, "end": v(-2, 50) * mm});
            skLineSegment(sketch, "E178", {"start": v(-10, 63.6) * mm, "end": v(-10, 65.4) * mm});
            skLineSegment(sketch, "E179", {"start": v(10, 65.4) * mm, "end": v(10, 63.6) * mm});
            skLineSegment(sketch, "E180.bottom", {"start": v(-1025, 50) * mm, "end": v(-1005, 50) * mm, "construction": true});
            skLineSegment(sketch, "E180.top", {"start": v(-1025, 68) * mm, "end": v(-1005, 68) * mm, "construction": true});
            skLineSegment(sketch, "E180.left", {"start": v(-1025, 50) * mm, "end": v(-1025, 68) * mm, "construction": true});
            skLineSegment(sketch, "E180.right", {"start": v(-1005, 50) * mm, "end": v(-1005, 68) * mm, "construction": true});
            skLineSegment(sketch, "E181", {"start": v(-1025, 64.5) * mm, "end": v(-1005, 64.5) * mm, "construction": true});
            skPoint(sketch, "E182", {"position": v(-1015, 64.5) * mm});
            skLineSegment(sketch, "E183.rect.bottom", {"start": v(20, 67.5) * mm, "end": v(-1025, 67.5) * mm, "construction": true});
            skLineSegment(sketch, "E183.rect.top", {"start": v(-1005, 61.5) * mm, "end": v(-2050, 61.5) * mm, "construction": true});
            skArc(sketch, "E184", {"start": v(-1025, 65.4) * mm, "mid": v(-1023.52, 66.02) * mm, "end": v(-1022.9, 67.5) * mm});
            skArc(sketch, "E185.0.MirrorCS", {"start": v(-1025, 63.6) * mm, "mid": v(-1023.52, 62.98) * mm, "end": v(-1022.9, 61.5) * mm});
            skLineSegment(sketch, "E186", {"start": v(-1015, 64.5) * mm, "end": v(-1015, 50) * mm, "construction": true});
            skArc(sketch, "E187.0.MirrorCS", {"start": v(-1005, 63.6) * mm, "mid": v(-1006.48, 62.98) * mm, "end": v(-1007.1, 61.5) * mm});
            skArc(sketch, "E187.1.MirrorCS", {"start": v(-1005, 65.4) * mm, "mid": v(-1006.48, 66.02) * mm, "end": v(-1007.1, 67.5) * mm});
            skLineSegment(sketch, "E188", {"start": v(-1022.9, 67.5) * mm, "end": v(-1022.4, 68) * mm});
            skLineSegment(sketch, "E189", {"start": v(-1022.4, 68) * mm, "end": v(-1007.6, 68) * mm});
            skLineSegment(sketch, "E190", {"start": v(-1007.6, 68) * mm, "end": v(-1007.1, 67.5) * mm});
            skPoint(sketch, "E191", {"position": v(-1015, 68) * mm});
            skLineSegment(sketch, "E192.bottom", {"start": v(-1021.55, 60.5) * mm, "end": v(-1008.45, 60.5) * mm, "construction": true});
            skLineSegment(sketch, "E192.top", {"start": v(-1021.55, 57.5) * mm, "end": v(-1008.45, 57.5) * mm, "construction": true});
            skLineSegment(sketch, "E192.left", {"start": v(-1021.55, 60.5) * mm, "end": v(-1021.55, 57.5) * mm, "construction": true});
            skLineSegment(sketch, "E192.right", {"start": v(-1008.45, 60.5) * mm, "end": v(-1008.45, 57.5) * mm, "construction": true});
            skPoint(sketch, "E193", {"position": v(-1015, 57.5) * mm});
            skLineSegment(sketch, "E194", {"start": v(-1022.9, 61.5) * mm, "end": v(-1021.55, 60.5) * mm});
            skLineSegment(sketch, "E195", {"start": v(-1008.45, 60.5) * mm, "end": v(-1007.1, 61.5) * mm});
            skLineSegment(sketch, "E196", {"start": v(-1008.45, 60.5) * mm, "end": v(-1008.45, 57.5) * mm});
            skLineSegment(sketch, "E197", {"start": v(-1021.55, 57.5) * mm, "end": v(-1021.55, 60.5) * mm});
            skLineSegment(sketch, "E198", {"start": v(-1025, 54) * mm, "end": v(-1025, 50.5) * mm});
            skLineSegment(sketch, "E199", {"start": v(-1024.5, 50) * mm, "end": v(-1017, 50) * mm});
            skLineSegment(sketch, "E200", {"start": v(-1005, 50.5) * mm, "end": v(-1005, 54) * mm});
            skLineSegment(sketch, "E201", {"start": v(-1021.55, 57.5) * mm, "end": v(-1025, 54) * mm});
            skLineSegment(sketch, "E202", {"start": v(-1005, 54) * mm, "end": v(-1008.45, 57.5) * mm});
            skCircle(sketch, "E203", {"center": v(-1025, 50) * mm, "radius": 0.5 * mm, "construction": true});
            skCircle(sketch, "E204", {"center": v(-1005, 50) * mm, "radius": 0.5 * mm, "construction": true});
            skLineSegment(sketch, "E205", {"start": v(-1025, 50.5) * mm, "end": v(-1024.5, 50) * mm});
            skLineSegment(sketch, "E206", {"start": v(-1005, 50.5) * mm, "end": v(-1005.5, 50) * mm});
            skLineSegment(sketch, "E207.trimOffspring", {"start": v(-1013, 50) * mm, "end": v(-1005.5, 50) * mm});
            skLineSegment(sketch, "E208", {"start": v(-1016.5, 50.5) * mm, "end": v(-1013.5, 50.5) * mm});
            skPoint(sketch, "E209", {"position": v(-1015, 50.5) * mm});
            skLineSegment(sketch, "E210", {"start": v(-1013, 50) * mm, "end": v(-1013.5, 50.5) * mm});
            skLineSegment(sketch, "E211", {"start": v(-1016.5, 50.5) * mm, "end": v(-1017, 50) * mm});
            skLineSegment(sketch, "E212", {"start": v(-1025, 63.6) * mm, "end": v(-1025, 65.4) * mm});
            skLineSegment(sketch, "E213", {"start": v(-1005, 65.4) * mm, "end": v(-1005, 63.6) * mm});
            skSolve(sketch);
        }
        {
            var Q0;
            Q0=makeQuery(id+"F41.imprint","IMPRINT",FACE,{"disambiguationData":[TD([[makeQuery(id+"F41.imprint","IMPRINT",EDGE,{"derivedFrom":sQuery(id+"F41.wireOp",EDGE,"E184")}),-1.0]])]});
            var Q1;
            Q1=makeQuery(id+"F41.imprint","IMPRINT",FACE,{"disambiguationData":[TD([[makeQuery(id+"F41.imprint","IMPRINT",EDGE,{"derivedFrom":sQuery(id+"F41.wireOp",EDGE,"E150")}),-1.0]])]});
            var Q2;
            Q2=makeQuery(id+"F2.opExtrude","CAP_FACE",FACE,{"disambiguationData":[OSD([sQuery(id+"F1.wireOp",EDGE,"E6.rect.bottom"),sQuery(id+"F1.wireOp",EDGE,"E6.rect.top"),sQuery(id+"F1.wireOp",EDGE,"E6.rect.left"),sQuery(id+"F1.wireOp",EDGE,"E6.rect.right"),sQuery(id+"F1.wireOp",EDGE,"E7.filletArc"),sQuery(id+"F1.wireOp",EDGE,"E8.filletArc"),sQuery(id+"F1.wireOp",EDGE,"E9.filletArc"),sQuery(id+"F1.wireOp",EDGE,"E10.filletArc"),sQuery(id+"F1.wireOp",EDGE,"E11.0"),sQuery(id+"F1.wireOp",EDGE,"E11.1"),sQuery(id+"F1.wireOp",EDGE,"E11.2"),sQuery(id+"F1.wireOp",EDGE,"E11.3")])],"isStart":true});
            extrude(context, id + "F42", {"entities" : qUnion([Q0, Q1]), "endBound" : BoundingType.UP_TO_SURFACE, "oppositeDirection" : true, "endBoundEntityFace" : qUnion([Q2]), "depth" : 25 * mm});
        }
        {
            var Q0;
            Q0=makeQuery(id+"F39.boolean.opBoolean","MERGE",FACE,{"derivedFrom":[makeQuery(id+"F19.opExtrude","SWEPT_FACE",FACE,{"disambiguationData":[OSD([sQuery(id+"F18.wireOp",EDGE,"E67.bottom")])]}),makeQuery(id+"F26.boolean.opBoolean","MERGE",FACE,{"derivedFrom":[makeQuery(id+"F5.opExtrude","SWEPT_FACE",FACE,{"disambiguationData":[OSD([sQuery(id+"F4.wireOp",EDGE,"E12.bottom")])]}),makeQuery(id+"F26.opExtrude","SWEPT_FACE",FACE,{"disambiguationData":[OSD([sQuery(id+"F25.wireOp",EDGE,"E91.bottom")])]}),makeQuery(id+"F26.opExtrude","SWEPT_FACE",FACE,{"disambiguationData":[OSD([sQuery(id+"F25.wireOp",EDGE,"E93.bottom")])]})]}),makeQuery(id+"F39.opExtrude","SWEPT_FACE",FACE,{"disambiguationData":[OSD([sQuery(id+"F38.wireOp",EDGE,"E137.bottom")])]})]});
            cPlane(context, id + "F43", {"entities" : qUnion([Q0]), "cplaneType" : CPlaneType.OFFSET, "offset" : 0 * mm, "width" : 150 * mm, "height" : 150 * mm});
        }
        {
            var Q0;
            Q0=qCreatedBy(id+"F43.planeOp",FACE);
            var sketch = newSketch(context, id + "F44", { "sketchPlane" : qUnion([Q0])});
            skPoint(sketch, "E214.0", {"position": v(220, -1040) * mm});
            skPoint(sketch, "E215.0", {"position": v(1755, -990) * mm});
            skLineSegment(sketch, "E216.bottom", {"start": v(1755, -990) * mm, "end": v(220, -990) * mm, "construction": true});
            skLineSegment(sketch, "E216.top", {"start": v(1755, -1040) * mm, "end": v(220, -1040) * mm, "construction": true});
            skLineSegment(sketch, "E216.left", {"start": v(1755, -990) * mm, "end": v(1755, -1040) * mm, "construction": true});
            skLineSegment(sketch, "E216.right", {"start": v(220, -990) * mm, "end": v(220, -1040) * mm, "construction": true});
            skLineSegment(sketch, "E217.0", {"start": v(696.67, -1040) * mm, "end": v(696.67, -532.5) * mm, "construction": true});
            skLineSegment(sketch, "E218.0", {"start": v(746.67, -1040) * mm, "end": v(746.67, -532.5) * mm, "construction": true});
            skPoint(sketch, "E219.orphan", {"position": v(696.67, -940) * mm});
            skPoint(sketch, "E220.orphan", {"position": v(746.67, -940) * mm});
            skLineSegment(sketch, "E221.bottom", {"start": v(701.67, -990) * mm, "end": v(741.67, -990) * mm});
            skLineSegment(sketch, "E221.top", {"start": v(701.67, -1040) * mm, "end": v(741.67, -1040) * mm});
            skLineSegment(sketch, "E221.left", {"start": v(696.67, -995) * mm, "end": v(696.67, -1035) * mm});
            skLineSegment(sketch, "E221.right", {"start": v(746.67, -995) * mm, "end": v(746.67, -1035) * mm});
            skLineSegment(sketch, "E222.0", {"start": v(1223.33, -1040) * mm, "end": v(1223.33, -532.5) * mm, "construction": true});
            skLineSegment(sketch, "E223.0", {"start": v(1273.33, -1040) * mm, "end": v(1273.33, -532.5) * mm, "construction": true});
            skPoint(sketch, "E224.orphan", {"position": v(1223.33, -940) * mm});
            skPoint(sketch, "E225.orphan", {"position": v(1273.33, -940) * mm});
            skLineSegment(sketch, "E226.bottom", {"start": v(1228.33, -990) * mm, "end": v(1268.33, -990) * mm});
            skLineSegment(sketch, "E226.top", {"start": v(1228.33, -1040) * mm, "end": v(1268.33, -1040) * mm});
            skLineSegment(sketch, "E226.left", {"start": v(1223.33, -995) * mm, "end": v(1223.33, -1035) * mm});
            skLineSegment(sketch, "E226.right", {"start": v(1273.33, -995) * mm, "end": v(1273.33, -1035) * mm});
            skPoint(sketch, "E227.0", {"position": v(215, -25) * mm});
            skPoint(sketch, "E228.0", {"position": v(1750, 25) * mm});
            skLineSegment(sketch, "E229.bottom", {"start": v(1750, 25) * mm, "end": v(215, 25) * mm, "construction": true});
            skLineSegment(sketch, "E229.top", {"start": v(1750, -25) * mm, "end": v(215, -25) * mm, "construction": true});
            skLineSegment(sketch, "E229.left", {"start": v(1750, 25) * mm, "end": v(1750, -25) * mm, "construction": true});
            skLineSegment(sketch, "E229.right", {"start": v(215, 25) * mm, "end": v(215, -25) * mm, "construction": true});
            skLineSegment(sketch, "E230.0", {"start": v(696.67, -482.5) * mm, "end": v(696.67, 25) * mm, "construction": true});
            skLineSegment(sketch, "E231.0", {"start": v(746.67, -482.5) * mm, "end": v(746.67, 25) * mm, "construction": true});
            skPoint(sketch, "E232.orphan", {"position": v(746.67, -75) * mm});
            skPoint(sketch, "E233.orphan", {"position": v(696.67, -75) * mm});
            skLineSegment(sketch, "E234.bottom", {"start": v(701.67, 25) * mm, "end": v(741.67, 25) * mm});
            skLineSegment(sketch, "E234.top", {"start": v(701.67, -25) * mm, "end": v(741.67, -25) * mm});
            skLineSegment(sketch, "E234.left", {"start": v(696.67, 20) * mm, "end": v(696.67, -20) * mm});
            skLineSegment(sketch, "E234.right", {"start": v(746.67, 20) * mm, "end": v(746.67, -20) * mm});
            skLineSegment(sketch, "E235.0", {"start": v(1273.33, -482.5) * mm, "end": v(1273.33, 25) * mm, "construction": true});
            skLineSegment(sketch, "E236.0", {"start": v(1223.33, -482.5) * mm, "end": v(1223.33, 25) * mm, "construction": true});
            skPoint(sketch, "E237.orphan", {"position": v(1223.33, -75) * mm});
            skPoint(sketch, "E238.orphan", {"position": v(1273.33, -75) * mm});
            skLineSegment(sketch, "E239.bottom", {"start": v(1228.33, 25) * mm, "end": v(1268.33, 25) * mm});
            skLineSegment(sketch, "E239.top", {"start": v(1228.33, -25) * mm, "end": v(1268.33, -25) * mm});
            skLineSegment(sketch, "E239.left", {"start": v(1223.33, 20) * mm, "end": v(1223.33, -20) * mm});
            skLineSegment(sketch, "E239.right", {"start": v(1273.33, 20) * mm, "end": v(1273.33, -20) * mm});
            skPoint(sketch, "E240.visualSharp", {"position": v(696.67, -990) * mm});
            skArc(sketch, "E240.filletArc", {"start": v(701.67, -990) * mm, "mid": v(698.13, -991.46) * mm, "end": v(696.67, -995) * mm});
            skPoint(sketch, "E241.visualSharp", {"position": v(746.67, -990) * mm});
            skArc(sketch, "E241.filletArc", {"start": v(746.67, -995) * mm, "mid": v(745.2, -991.46) * mm, "end": v(741.67, -990) * mm});
            skPoint(sketch, "E242.visualSharp", {"position": v(696.67, -1040) * mm});
            skArc(sketch, "E242.filletArc", {"start": v(696.67, -1035) * mm, "mid": v(698.13, -1038.54) * mm, "end": v(701.67, -1040) * mm});
            skPoint(sketch, "E243.visualSharp", {"position": v(746.67, -1040) * mm});
            skArc(sketch, "E243.filletArc", {"start": v(741.67, -1040) * mm, "mid": v(745.2, -1038.54) * mm, "end": v(746.67, -1035) * mm});
            skPoint(sketch, "E244.visualSharp", {"position": v(1223.33, -990) * mm});
            skArc(sketch, "E244.filletArc", {"start": v(1228.33, -990) * mm, "mid": v(1224.8, -991.46) * mm, "end": v(1223.33, -995) * mm});
            skPoint(sketch, "E245.visualSharp", {"position": v(1273.33, -990) * mm});
            skArc(sketch, "E245.filletArc", {"start": v(1273.33, -995) * mm, "mid": v(1271.87, -991.46) * mm, "end": v(1268.33, -990) * mm});
            skPoint(sketch, "E246.visualSharp", {"position": v(1273.33, -1040) * mm});
            skArc(sketch, "E246.filletArc", {"start": v(1268.33, -1040) * mm, "mid": v(1271.87, -1038.54) * mm, "end": v(1273.33, -1035) * mm});
            skPoint(sketch, "E247.visualSharp", {"position": v(1223.33, -1040) * mm});
            skArc(sketch, "E247.filletArc", {"start": v(1223.33, -1035) * mm, "mid": v(1224.8, -1038.54) * mm, "end": v(1228.33, -1040) * mm});
            skPoint(sketch, "E248.visualSharp", {"position": v(696.67, 25) * mm});
            skArc(sketch, "E248.filletArc", {"start": v(701.67, 25) * mm, "mid": v(698.13, 23.54) * mm, "end": v(696.67, 20) * mm});
            skPoint(sketch, "E249.visualSharp", {"position": v(746.67, 25) * mm});
            skArc(sketch, "E249.filletArc", {"start": v(746.67, 20) * mm, "mid": v(745.2, 23.54) * mm, "end": v(741.67, 25) * mm});
            skPoint(sketch, "E250.visualSharp", {"position": v(746.67, -25) * mm});
            skArc(sketch, "E250.filletArc", {"start": v(741.67, -25) * mm, "mid": v(745.2, -23.54) * mm, "end": v(746.67, -20) * mm});
            skPoint(sketch, "E251.visualSharp", {"position": v(696.67, -25) * mm});
            skArc(sketch, "E251.filletArc", {"start": v(696.67, -20) * mm, "mid": v(698.13, -23.54) * mm, "end": v(701.67, -25) * mm});
            skPoint(sketch, "E252.visualSharp", {"position": v(1223.33, 25) * mm});
            skArc(sketch, "E252.filletArc", {"start": v(1228.33, 25) * mm, "mid": v(1224.8, 23.54) * mm, "end": v(1223.33, 20) * mm});
            skPoint(sketch, "E253.visualSharp", {"position": v(1273.33, 25) * mm});
            skArc(sketch, "E253.filletArc", {"start": v(1273.33, 20) * mm, "mid": v(1271.87, 23.54) * mm, "end": v(1268.33, 25) * mm});
            skPoint(sketch, "E254.visualSharp", {"position": v(1273.33, -25) * mm});
            skArc(sketch, "E254.filletArc", {"start": v(1268.33, -25) * mm, "mid": v(1271.87, -23.54) * mm, "end": v(1273.33, -20) * mm});
            skPoint(sketch, "E255.visualSharp", {"position": v(1223.33, -25) * mm});
            skArc(sketch, "E255.filletArc", {"start": v(1223.33, -20) * mm, "mid": v(1224.8, -23.54) * mm, "end": v(1228.33, -25) * mm});
            skSolve(sketch);
        }
        {
            var Q0;
            Q0=makeQuery(id+"F44.imprint","IMPRINT",FACE,{"disambiguationData":[TD([[makeQuery(id+"F44.imprint","IMPRINT",EDGE,{"derivedFrom":sQuery(id+"F44.wireOp",EDGE,"E234.bottom")}),-1.0]])]});
            var Q1;
            Q1=makeQuery(id+"F44.imprint","IMPRINT",FACE,{"disambiguationData":[TD([[makeQuery(id+"F44.imprint","IMPRINT",EDGE,{"derivedFrom":sQuery(id+"F44.wireOp",EDGE,"E239.bottom")}),-1.0]])]});
            var Q2;
            Q2=makeQuery(id+"F44.imprint","IMPRINT",FACE,{"disambiguationData":[TD([[makeQuery(id+"F44.imprint","IMPRINT",EDGE,{"derivedFrom":sQuery(id+"F44.wireOp",EDGE,"E226.bottom")}),-1.0]])]});
            var Q3;
            Q3=makeQuery(id+"F44.imprint","IMPRINT",FACE,{"disambiguationData":[TD([[makeQuery(id+"F44.imprint","IMPRINT",EDGE,{"derivedFrom":sQuery(id+"F44.wireOp",EDGE,"E221.bottom")}),-1.0]])]});
            var Q4;
            {var subQ0=sQuery(id+"F1.wireOp",EDGE,"E6.rect.top");var subQ5=sQuery(id+"F7.wireOp",EDGE,"E29.left");var subQ6=makeQuery(id+"F8.opExtrude","SWEPT_FACE",FACE,{"disambiguationData":[OSD([subQ5])]});Q4=makeQuery(id+"F12.boolean.opBoolean","SPLIT",FACE,{"disambiguationData":[TD([subQ6])],"derivedFrom":makeQuery(id+"F8.boolean.opBoolean","SPLIT",FACE,{"disambiguationData":[TD([subQ6])],"derivedFrom":makeQuery(id+"F2.opExtrude","SWEPT_FACE",FACE,{"disambiguationData":[OSD([subQ0])]})})});}
            extrude(context, id + "F45", {"entities" : qUnion([Q0, Q1, Q2, Q3]), "operationType" : NewBodyOperationType.ADD, "endBound" : BoundingType.UP_TO_SURFACE, "endBoundEntityFace" : qUnion([Q4]), "depth" : 25 * mm});
        }
        {
            var Q0;
            Q0=makeQuery(id+"F31.opExtrude","SWEPT_FACE",FACE,{"disambiguationData":[OSD([sQuery(id+"F30.wireOp",EDGE,"E113.left")])]});
            cPlane(context, id + "F46", {"entities" : qUnion([Q0]), "cplaneType" : CPlaneType.OFFSET, "offset" : 50 * mm, "width" : 150 * mm, "height" : 150 * mm});
        }
        {
            var Q0;
            Q0=qCreatedBy(id+"F46.planeOp",FACE);
            var sketch = newSketch(context, id + "F47", { "sketchPlane" : qUnion([Q0])});
            skPoint(sketch, "E256.0", {"position": v(215, -1000) * mm});
            skPoint(sketch, "E257.0", {"position": v(1755, -950) * mm});
            skLineSegment(sketch, "E258.bottom", {"start": v(1755, -950) * mm, "end": v(215, -950) * mm, "construction": true});
            skLineSegment(sketch, "E258.top", {"start": v(1755, -1000) * mm, "end": v(215, -1000) * mm, "construction": true});
            skLineSegment(sketch, "E258.left", {"start": v(1755, -950) * mm, "end": v(1755, -1000) * mm, "construction": true});
            skLineSegment(sketch, "E258.right", {"start": v(215, -950) * mm, "end": v(215, -1000) * mm, "construction": true});
            skLineSegment(sketch, "E259.0", {"start": v(960, -200) * mm, "end": v(960, -1000) * mm, "construction": true});
            skLineSegment(sketch, "E260.0", {"start": v(1010, -200) * mm, "end": v(1010, -1000) * mm, "construction": true});
            skPoint(sketch, "E261.orphan", {"position": v(960, -950) * mm});
            skPoint(sketch, "E262.orphan", {"position": v(1010, -950) * mm});
            skLineSegment(sketch, "E263.bottom", {"start": v(965, -950) * mm, "end": v(1005, -950) * mm});
            skLineSegment(sketch, "E263.top", {"start": v(965, -1000) * mm, "end": v(1005, -1000) * mm});
            skLineSegment(sketch, "E263.left", {"start": v(960, -955) * mm, "end": v(960, -995) * mm});
            skLineSegment(sketch, "E263.right", {"start": v(1010, -955) * mm, "end": v(1010, -995) * mm});
            skArc(sketch, "E264.filletArc", {"start": v(965, -950) * mm, "mid": v(961.46, -951.46) * mm, "end": v(960, -955) * mm});
            skArc(sketch, "E265.filletArc", {"start": v(1010, -955) * mm, "mid": v(1008.54, -951.46) * mm, "end": v(1005, -950) * mm});
            skPoint(sketch, "E266.visualSharp", {"position": v(1010, -1000) * mm});
            skArc(sketch, "E266.filletArc", {"start": v(1005, -1000) * mm, "mid": v(1008.54, -998.54) * mm, "end": v(1010, -995) * mm});
            skPoint(sketch, "E267.visualSharp", {"position": v(960, -1000) * mm});
            skArc(sketch, "E267.filletArc", {"start": v(960, -995) * mm, "mid": v(961.46, -998.54) * mm, "end": v(965, -1000) * mm});
            skSolve(sketch);
        }
        {
            var Q0;
            Q0 = qSketchRegion(id + "F47", true);
            var Q1;
            Q1=makeQuery(id+"F34.boolean.opBoolean","MERGE",FACE,{"derivedFrom":[makeQuery(id+"F29.opExtrude","SWEPT_FACE",FACE,{"disambiguationData":[OSD([sQuery(id+"F28.wireOp",EDGE,"E106.left")])]}),makeQuery(id+"F34.opExtrude","SWEPT_FACE",FACE,{"disambiguationData":[OSD([sQuery(id+"F33.wireOp",EDGE,"E122.top")])]})]});
            extrude(context, id + "F48", {"entities" : qUnion([Q0]), "operationType" : NewBodyOperationType.ADD, "endBound" : BoundingType.UP_TO_NEXT, "endBoundEntity" : qUnion([Q1]), "depth" : 25 * mm, "hasSecondDirection" : true, "secondDirectionBound" : SecondDirectionBoundingType.UP_TO_NEXT, "secondDirectionOppositeDirection" : true, "secondDirectionDepth" : 25 * mm});
        }
    });
